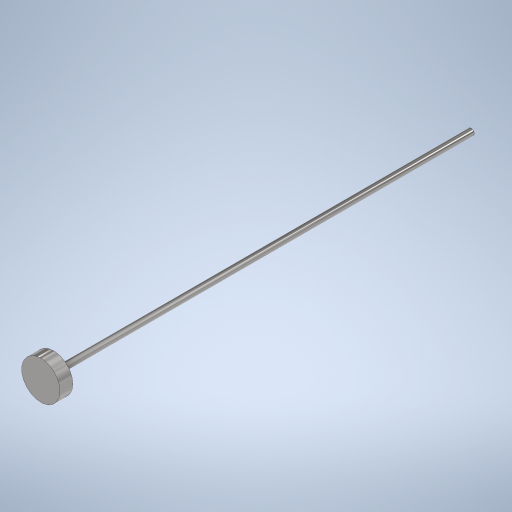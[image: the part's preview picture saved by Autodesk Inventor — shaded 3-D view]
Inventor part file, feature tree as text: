
AUTODESK INVENTOR PART (.ipt)
format: ipt  version: 2023.2 (Build 272271000, 271)  size: 261,120 bytes
history: native  units: mm
features: extrude x2, sketch x2
ambient origin geometry x8: Origin, YZ Plane, XZ Plane, XY Plane, X Axis, Y Axis, Z Axis, Center Point
bodies: Solid1 (feature_tree)
feature tree (4):
  extrude  "Extrusion1"  Depth=98.0mm TaperAngle=0.0deg
  extrude  "Extrusion2"  Depth=3.0mm TaperAngle=0.0deg
  sketch  "Sketch1"  dims[d0=1.5mm d1=98.0mm d2=0.0mm]
  sketch  "Sketch2"  dims[d3=9.0mm d4=3.0mm d5=0.0mm]
